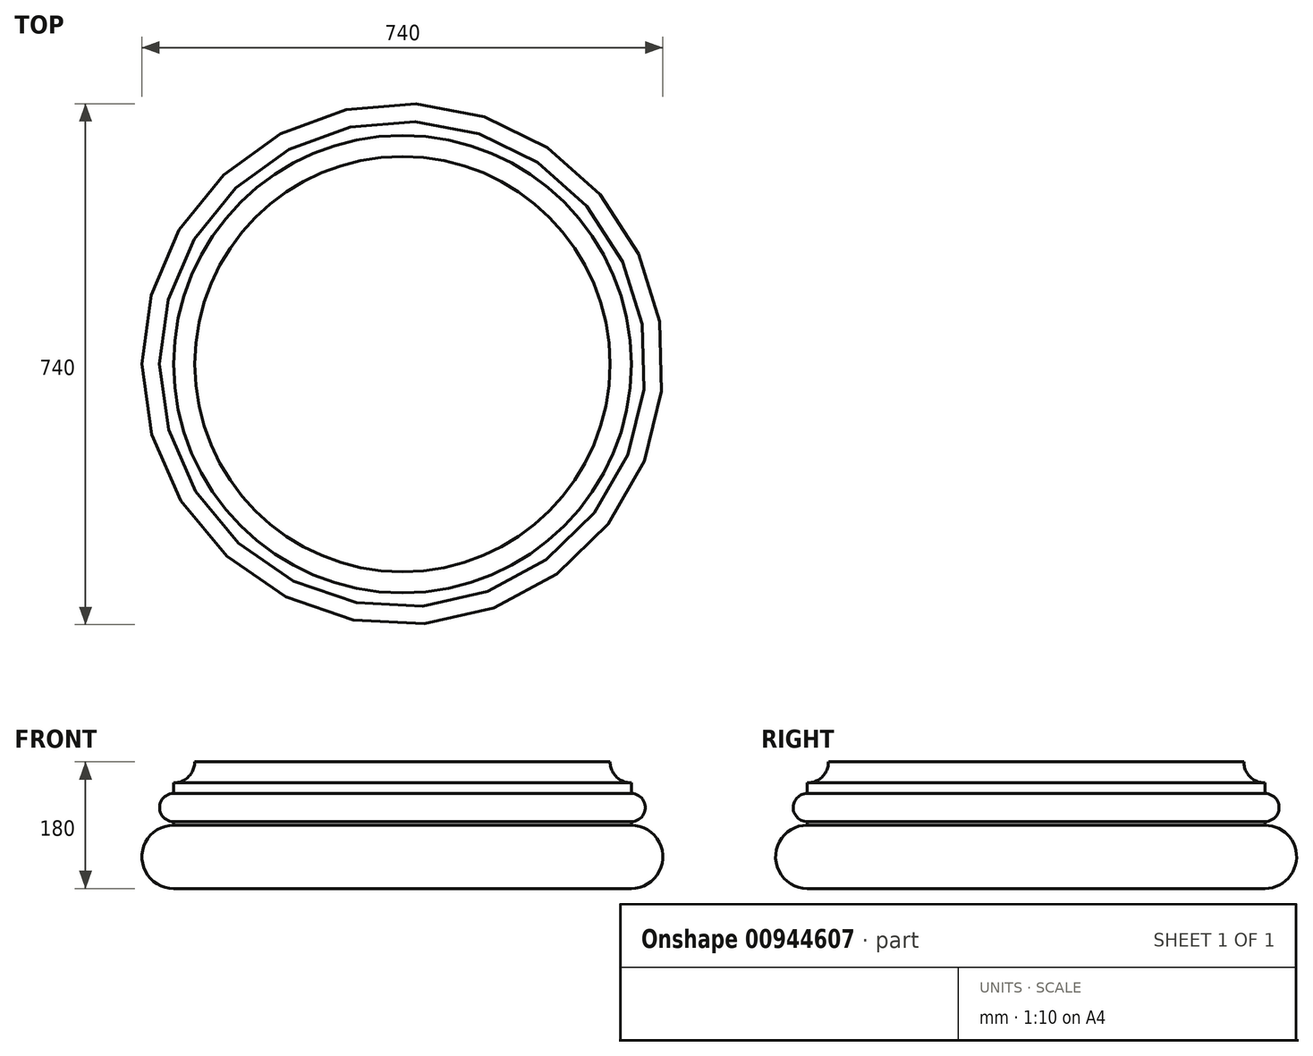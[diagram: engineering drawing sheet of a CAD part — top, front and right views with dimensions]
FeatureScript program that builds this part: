
annotation { "Feature Type Name" : "Feature", "Feature Type Description" : "" }
export const myFeature = defineFeature(function(context is Context, id is Id, definition is map)
    precondition{}
    {
        {
            var Q0;
            Q0=qCreatedBy(makeId("Front.planeOp"),FACE);
            var sketch = newSketch(context, id + "F0", { "sketchPlane" : qUnion([Q0])});
            skLineSegment(sketch, "E0", {"start": v(0, 0) * mm, "end": v(-325, 0) * mm});
            skArc(sketch, "E1", {"start": v(-325, 0) * mm, "mid": v(-370, 45) * mm, "end": v(-325, 90) * mm});
            skLineSegment(sketch, "E2", {"start": v(-325, 90) * mm, "end": v(-325, 95) * mm});
            skArc(sketch, "E3", {"start": v(-325, 135) * mm, "mid": v(-345, 115) * mm, "end": v(-325, 95) * mm});
            skLineSegment(sketch, "E4", {"start": v(-325, 135) * mm, "end": v(-325, 150) * mm});
            skArc(sketch, "E5", {"start": v(-295, 180) * mm, "mid": v(-303.79, 158.79) * mm, "end": v(-325, 150) * mm});
            skLineSegment(sketch, "E6", {"start": v(0, 0) * mm, "end": v(0, 180) * mm});
            skLineSegment(sketch, "E7", {"start": v(-295, 180) * mm, "end": v(0, 180) * mm});
            skSolve(sketch);
        }
        {
            var Q0;
            Q0=makeQuery(id+"F0.imprint","IMPRINT",FACE,{"disambiguationData":[TD([[makeQuery(id+"F0.imprint","IMPRINT",EDGE,{"derivedFrom":sQuery(id+"F0.wireOp",EDGE,"E0")}),-1.0]])]});
            var Q1;
            Q1=sQuery(id+"F0.wireOp",EDGE,"E6");
            revolve(context, id + "F1", {"surfaceOperationType" : NewSurfaceOperationType.NEW, "entities" : qUnion([Q0]), "axis" : qUnion([Q1]), "revolveType" : RevolveType.FULL});
        }
    });
